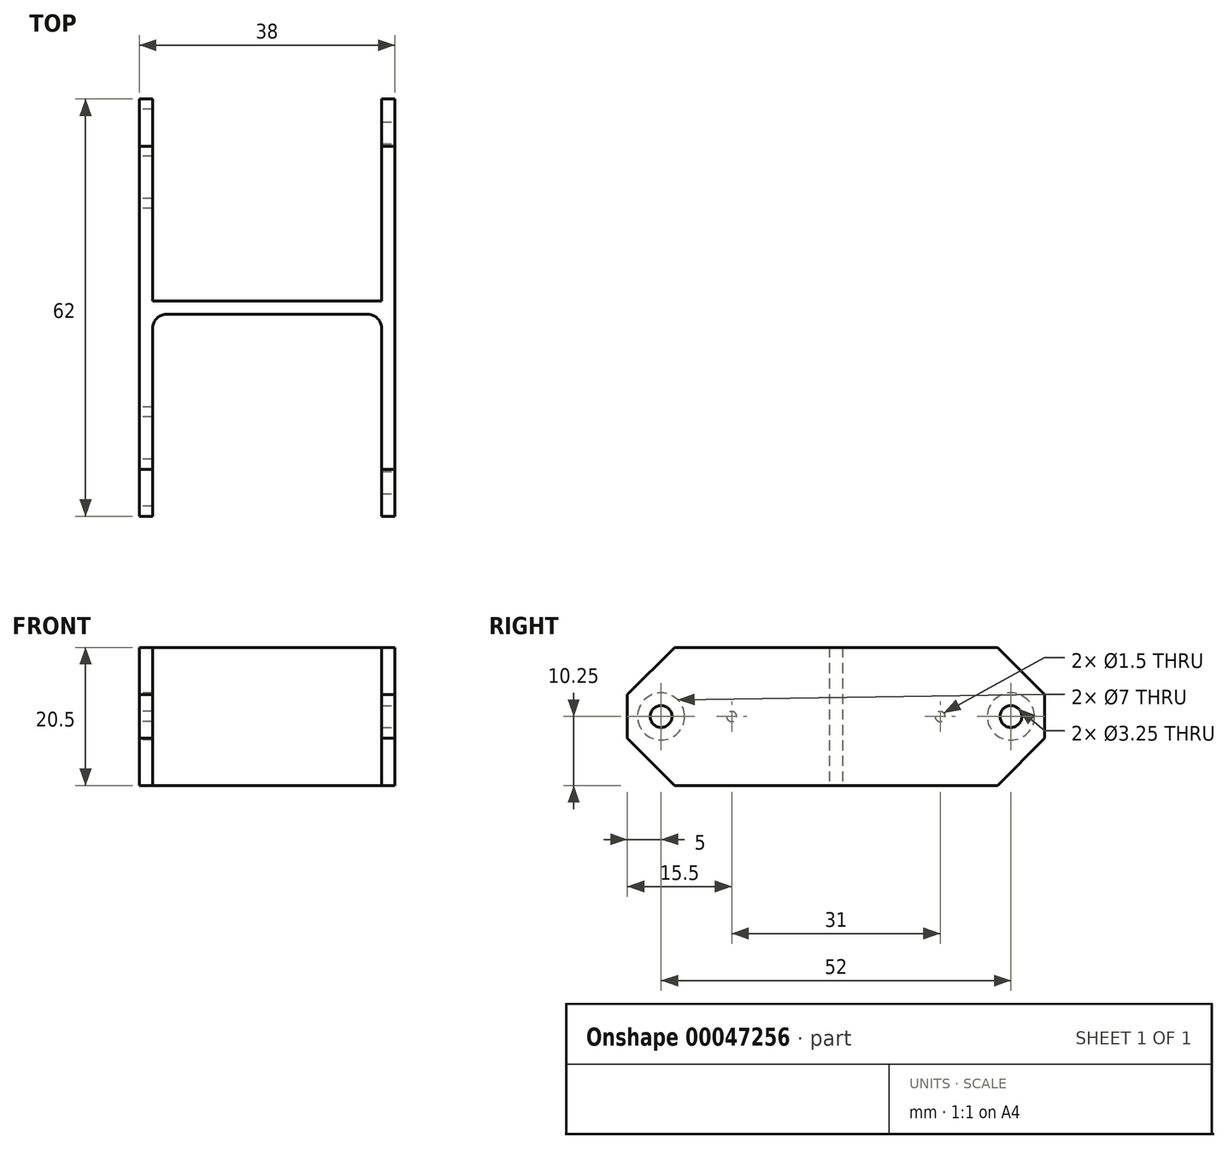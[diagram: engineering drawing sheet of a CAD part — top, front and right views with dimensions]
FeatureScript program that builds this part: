
annotation { "Feature Type Name" : "Feature", "Feature Type Description" : "" }
export const myFeature = defineFeature(function(context is Context, id is Id, definition is map)
    precondition{}
    {
        {
            var Q0;
            Q0=qCreatedBy(makeId("Top.planeOp"),FACE);
            var sketch = newSketch(context, id + "F0", { "sketchPlane" : qUnion([Q0])});
            skLineSegment(sketch, "E0", {"start": v(0, 0) * mm, "end": v(34, 0) * mm, "construction": true});
            skLineSegment(sketch, "E1", {"start": v(0, 0) * mm, "end": v(0, 30) * mm});
            skLineSegment(sketch, "E2", {"start": v(0, 30) * mm, "end": v(34, 30) * mm});
            skLineSegment(sketch, "E3", {"start": v(34, 30) * mm, "end": v(34, 0) * mm});
            skLineSegment(sketch, "E4.0", {"start": v(36, 32) * mm, "end": v(36, 0) * mm});
            skLineSegment(sketch, "E4.1", {"start": v(-2, 32) * mm, "end": v(36, 32) * mm});
            skLineSegment(sketch, "E4.2", {"start": v(-2, 0) * mm, "end": v(-2, 32) * mm});
            skLineSegment(sketch, "E5", {"start": v(-2, 0) * mm, "end": v(0, 0) * mm});
            skLineSegment(sketch, "E6", {"start": v(34, 0) * mm, "end": v(36, 0) * mm});
            skSolve(sketch);
        }
        {
            var Q0;
            Q0=qSketchRegion(id+"F0",true);
            extrude(context, id + "F1", {"entities" : qUnion([Q0]), "depth" : 20.5 * mm});
        }
        {
            var Q0;
            Q0=makeQuery(id+"F1.opExtrude","CAP_EDGE",EDGE,{"disambiguationData":[OSD([sQuery(id+"F0.wireOp",EDGE,"E5")])],"isStart":true});
            var Q1;
            Q1=makeQuery(id+"F1.opExtrude","CAP_EDGE",EDGE,{"disambiguationData":[OSD([sQuery(id+"F0.wireOp",EDGE,"E5")])],"isStart":false});
            var Q2;
            Q2=makeQuery(id+"F1.opExtrude","CAP_EDGE",EDGE,{"disambiguationData":[OSD([sQuery(id+"F0.wireOp",EDGE,"E6")])],"isStart":true});
            var Q3;
            Q3=makeQuery(id+"F1.opExtrude","CAP_EDGE",EDGE,{"disambiguationData":[OSD([sQuery(id+"F0.wireOp",EDGE,"E6")])],"isStart":false});
            chamfer(context, id + "F2", {"entities" : qUnion([Q0, Q1, Q2, Q3]), "width" : 7 * mm, "tangentPropagation" : true});
        }
        {
            var Q0;
            Q0=makeQuery(id+"F1.opExtrude","SWEPT_FACE",FACE,{"disambiguationData":[OSD([sQuery(id+"F0.wireOp",EDGE,"E4.2")])]});
            var sketch = newSketch(context, id + "F3", { "sketchPlane" : qUnion([Q0])});
            skLineSegment(sketch, "E7", {"start": v(0, 10.25) * mm, "end": v(-5, 10.25) * mm, "construction": true});
            skPoint(sketch, "E7.endSnap0", {"position": v(0, 10.25) * mm});
            skCircle(sketch, "E8", {"center": v(-5, 10.25) * mm, "radius": 3.5 * mm});
            skLineSegment(sketch, "E9", {"start": v(-5, 10.25) * mm, "end": v(-15.5, 10.25) * mm, "construction": true});
            skCircle(sketch, "E10", {"center": v(-15.5, 10.25) * mm, "radius": 0.75 * mm});
            skSolve(sketch);
        }
        {
            var Q0;
            Q0=qSketchRegion(id+"F3",true);
            extrude(context, id + "F4", {"entities" : qUnion([Q0]), "operationType" : NewBodyOperationType.REMOVE, "oppositeDirection" : true, "depth" : 25 * mm});
        }
        {
            var Q0;
            Q0=makeQuery(id+"F1.opExtrude","SWEPT_FACE",FACE,{"disambiguationData":[OSD([sQuery(id+"F0.wireOp",EDGE,"E4.0")])]});
            var sketch = newSketch(context, id + "F5", { "sketchPlane" : qUnion([Q0])});
            skCircle(sketch, "E11.0", {"center": v(5, 10.25) * mm, "radius": 3.5 * mm, "construction": true});
            skCircle(sketch, "E12", {"center": v(5, 10.25) * mm, "radius": 1.62 * mm});
            skSolve(sketch);
        }
        {
            var Q0;
            Q0=qSketchRegion(id+"F5",true);
            extrude(context, id + "F6", {"entities" : qUnion([Q0]), "operationType" : NewBodyOperationType.REMOVE, "oppositeDirection" : true, "depth" : 25 * mm});
        }
        {
            var Q0;
            Q0=makeQuery(id+"F1.opExtrude","SWEPT_FACE",FACE,{"disambiguationData":[OSD([sQuery(id+"F0.wireOp",EDGE,"E4.1")])]});
            cPlane(context, id + "F7", {"entities" : qUnion([Q0]), "cplaneType" : CPlaneType.OFFSET, "offset" : 1 * mm, "oppositeDirection" : true, "width" : 150 * mm, "height" : 150 * mm});
        }
        {
            var Q0;
            Q0=makeQuery(id+"F1.opExtrude","SWEPT_BODY",BODY,{"disambiguationData":[OSD([sQuery(id+"F0.wireOp",EDGE,"E1"),sQuery(id+"F0.wireOp",EDGE,"E2"),sQuery(id+"F0.wireOp",EDGE,"E3"),sQuery(id+"F0.wireOp",EDGE,"E4.0"),sQuery(id+"F0.wireOp",EDGE,"E4.1"),sQuery(id+"F0.wireOp",EDGE,"E4.2"),sQuery(id+"F0.wireOp",EDGE,"E5"),sQuery(id+"F0.wireOp",EDGE,"E6")])]});
            var Q1;
            Q1=qCreatedBy(id+"F7.planeOp",FACE);
            mirror(context, id + "F8", {"operationType" : NewBodyOperationType.ADD, "entities" : qUnion([Q0]), "mirrorPlane" : qUnion([Q1])});
        }
        {
            var Q0;
            Q0=makeQuery(id+"F1.opExtrude","SWEPT_EDGE",EDGE,{"disambiguationData":[OSD([sQuery(id+"F0.wireOp",EDGE,"E1"),sQuery(id+"F0.wireOp",EDGE,"E2")])]});
            var Q1;
            Q1=makeQuery(id+"F8.opPattern","COPY",EDGE,{"derivedFrom":makeQuery(id+"F1.opExtrude","SWEPT_EDGE",EDGE,{"disambiguationData":[OSD([sQuery(id+"F0.wireOp",EDGE,"E1"),sQuery(id+"F0.wireOp",EDGE,"E2")])]}),"instanceName":"1"});
            var Q2;
            Q2=makeQuery(id+"F8.opPattern","COPY",EDGE,{"derivedFrom":makeQuery(id+"F1.opExtrude","SWEPT_EDGE",EDGE,{"disambiguationData":[OSD([sQuery(id+"F0.wireOp",EDGE,"E2"),sQuery(id+"F0.wireOp",EDGE,"E3")])]}),"instanceName":"1"});
            var Q3;
            Q3=makeQuery(id+"F1.opExtrude","SWEPT_EDGE",EDGE,{"disambiguationData":[OSD([sQuery(id+"F0.wireOp",EDGE,"E2"),sQuery(id+"F0.wireOp",EDGE,"E3")])]});
            fillet(context, id + "F9", {"entities" : qUnion([Q0, Q1, Q2, Q3]), "radius" : 2 * mm, "tangentPropagation" : true, "allowEdgeOverflow" : false});
        }
    });
